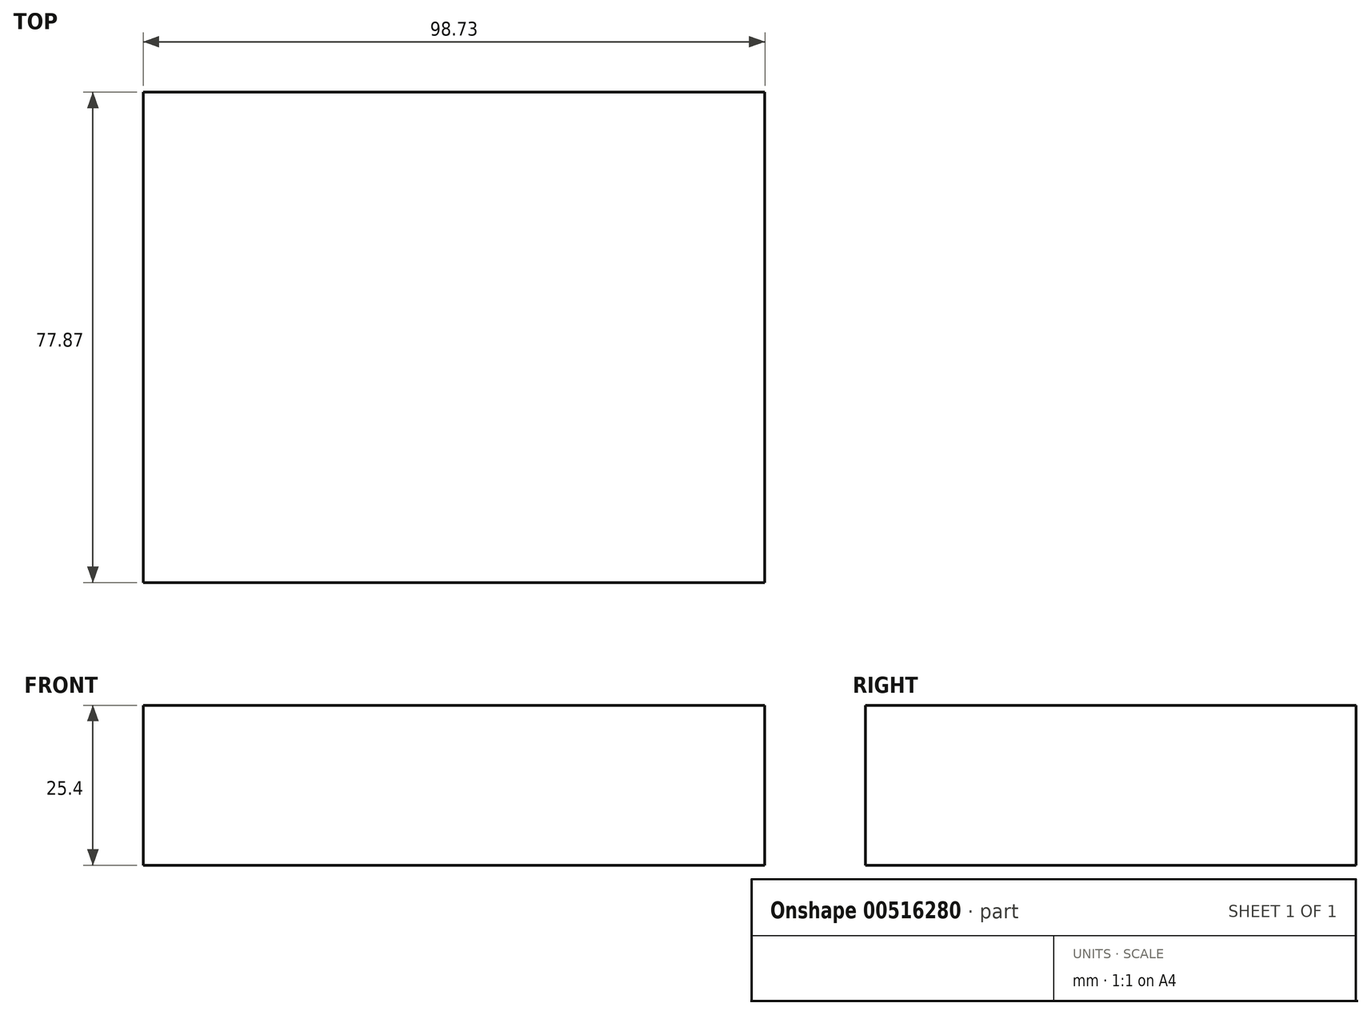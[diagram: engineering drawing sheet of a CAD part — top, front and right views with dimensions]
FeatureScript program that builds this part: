
annotation { "Feature Type Name" : "Feature", "Feature Type Description" : "" }
export const myFeature = defineFeature(function(context is Context, id is Id, definition is map)
    precondition{}
    {
        {
            var Q0;
            Q0=qCreatedBy(makeId("Top.planeOp"),FACE);
            var sketch = newSketch(context, id + "F0", { "sketchPlane" : qUnion([Q0])});
            skLineSegment(sketch, "E0.bottom", {"start": v(-54, 41.32) * mm, "end": v(44.72, 41.32) * mm});
            skLineSegment(sketch, "E0.top", {"start": v(-54, -36.55) * mm, "end": v(44.72, -36.55) * mm});
            skLineSegment(sketch, "E0.left", {"start": v(-54, 41.32) * mm, "end": v(-54, -36.55) * mm});
            skLineSegment(sketch, "E0.right", {"start": v(44.72, 41.32) * mm, "end": v(44.72, -36.55) * mm});
            skSolve(sketch);
        }
        {
            var Q0;
            Q0=makeQuery(id+"F0.imprint","IMPRINT",FACE,{"disambiguationData":[TD([[makeQuery(id+"F0.imprint","IMPRINT",EDGE,{"derivedFrom":sQuery(id+"F0.wireOp",EDGE,"E0.bottom")}),-1.0]])]});
            extrude(context, id + "F1", {"entities" : qUnion([Q0]), "depth" : 25.4 * mm, "offsetDistance" : 25.4 * mm});
        }
    });
